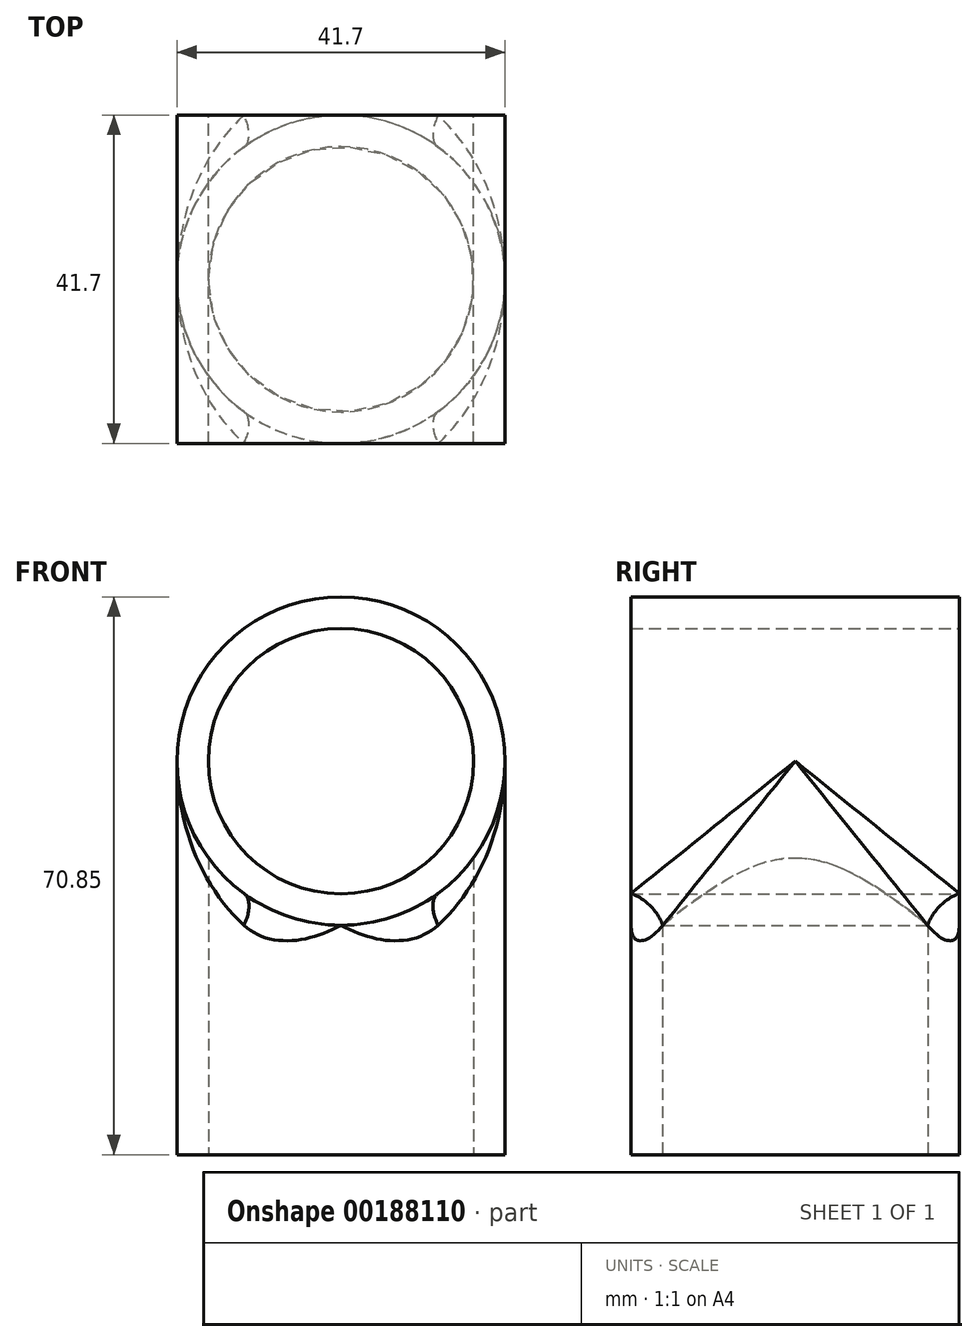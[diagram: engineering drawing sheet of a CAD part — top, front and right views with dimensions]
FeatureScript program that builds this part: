
annotation { "Feature Type Name" : "Feature", "Feature Type Description" : "" }
export const myFeature = defineFeature(function(context is Context, id is Id, definition is map)
    precondition{}
    {
        {
            var Q0;
            Q0=qCreatedBy(makeId("Top.planeOp"),FACE);
            var sketch = newSketch(context, id + "F0", { "sketchPlane" : qUnion([Q0])});
            skCircle(sketch, "E0", {"center": v(0, 0) * mm, "radius": 16.85 * mm});
            skCircle(sketch, "E1", {"center": v(0, 0) * mm, "radius": 20.85 * mm});
            skSolve(sketch);
        }
        {
            var Q0;
            Q0=makeQuery(id+"F0.imprint","IMPRINT",FACE,{"disambiguationData":[TD([[makeQuery(id+"F0.imprint","IMPRINT",EDGE,{"derivedFrom":sQuery(id+"F0.wireOp",EDGE,"E0")}),-1.0]])]});
            extrude(context, id + "F1", {"entities" : qUnion([Q0]), "depth" : 50 * mm});
        }
        {
            var Q0;
            Q0=makeQuery(id+"F1.opExtrude","CAP_FACE",FACE,{"disambiguationData":[OSD([sQuery(id+"F0.wireOp",EDGE,"E0"),sQuery(id+"F0.wireOp",EDGE,"E1")])],"isStart":false});
            var sketch = newSketch(context, id + "F2", { "sketchPlane" : qUnion([Q0])});
            skLineSegment(sketch, "E2.bottom", {"start": v(0, 20.85) * mm, "end": v(20.85, 20.85) * mm});
            skLineSegment(sketch, "E2.top", {"start": v(0, 0) * mm, "end": v(20.85, 0) * mm});
            skLineSegment(sketch, "E2.left", {"start": v(0, 20.85) * mm, "end": v(0, 0) * mm});
            skLineSegment(sketch, "E2.right", {"start": v(20.85, 20.85) * mm, "end": v(20.85, 0) * mm});
            skLineSegment(sketch, "E3.bottom", {"start": v(20.85, 0) * mm, "end": v(0, 0) * mm});
            skLineSegment(sketch, "E3.top", {"start": v(20.85, -20.85) * mm, "end": v(0, -20.85) * mm});
            skLineSegment(sketch, "E3.left", {"start": v(20.85, 0) * mm, "end": v(20.85, -20.85) * mm});
            skLineSegment(sketch, "E3.right", {"start": v(0, 0) * mm, "end": v(0, -20.85) * mm});
            skLineSegment(sketch, "E4", {"start": v(16.85, 0) * mm, "end": v(16.85, 20.85) * mm});
            skLineSegment(sketch, "E5", {"start": v(16.85, 0) * mm, "end": v(16.85, -20.85) * mm});
            skLineSegment(sketch, "E6", {"start": v(0, 20.85) * mm, "end": v(0, -20.85) * mm});
            skSolve(sketch);
        }
        {
            var Q0;
            {var subQ0=sQuery(id+"F2.wireOp",EDGE,"E2.right");Q0=makeQuery(id+"F2.imprint","IMPRINT",FACE,{"disambiguationData":[TD([[makeQuery(id+"F2.imprint","IMPRINT",EDGE,{"derivedFrom":subQ0}),-1.0]])]});}
            var Q1;
            {var subQ1=makeQuery(id+"F1.opExtrude","CAP_EDGE",EDGE,{"disambiguationData":[OSD([sQuery(id+"F0.wireOp",EDGE,"E1")])],"isStart":false});var subQ3=sQuery(id+"F2.wireOp",EDGE,"E4");var subQ5=makeQuery(id+"F2.imprint","INTERSECT",VERTEX,{"derivedFrom":[subQ1,subQ3]});Q1=makeQuery(id+"F2.imprint","IMPRINT",FACE,{"disambiguationData":[TD([[makeQuery(id+"F2.imprint","IMPRINT",EDGE,{"disambiguationData":[TD([[subQ5,1.0]])],"derivedFrom":subQ3}),-1.0]])]});}
            var Q2;
            {var subQ1=makeQuery(id+"F1.opExtrude","CAP_EDGE",EDGE,{"disambiguationData":[OSD([sQuery(id+"F0.wireOp",EDGE,"E1")])],"isStart":false});var subQ3=sQuery(id+"F2.wireOp",EDGE,"E5");var subQ5=makeQuery(id+"F2.imprint","INTERSECT",VERTEX,{"derivedFrom":[subQ1,subQ3]});Q2=makeQuery(id+"F2.imprint","IMPRINT",FACE,{"disambiguationData":[TD([[makeQuery(id+"F2.imprint","IMPRINT",EDGE,{"disambiguationData":[TD([[subQ5,1.0]])],"derivedFrom":subQ3}),1.0]])]});}
            var Q3;
            {var subQ0=sQuery(id+"F2.wireOp",EDGE,"E3.left");Q3=makeQuery(id+"F2.imprint","IMPRINT",FACE,{"disambiguationData":[TD([[makeQuery(id+"F2.imprint","IMPRINT",EDGE,{"derivedFrom":subQ0}),-1.0]])]});}
            var Q4;
            Q4=sQuery(id+"F2.wireOp",EDGE,"E6");
            revolve(context, id + "F3", {"operationType" : NewBodyOperationType.ADD, "entities" : qUnion([Q0, Q1, Q2, Q3]), "axis" : qUnion([Q4]), "revolveType" : RevolveType.FULL});
        }
        {
            var Q0;
            Q0=makeQuery(id+"F3.opRevolve","SWEPT_FACE",FACE,{"disambiguationData":[OSD([sQuery(id+"F2.wireOp",EDGE,"E2.bottom")])]});
            var sketch = newSketch(context, id + "F4", { "sketchPlane" : qUnion([Q0])});
            skCircle(sketch, "E7.0.0", {"center": v(0, 50) * mm, "radius": 20.85 * mm});
            skSolve(sketch);
        }
        {
            var Q0;
            Q0=makeQuery(id+"F4.imprint","IMPRINT",FACE,{"disambiguationData":[TD([[makeQuery(id+"F4.imprint","IMPRINT",EDGE,{"derivedFrom":makeQuery(id+"F3.opRevolve","SWEPT_EDGE",EDGE,{"disambiguationData":[OSD([sQuery(id+"F2.wireOp",EDGE,"E2.bottom"),sQuery(id+"F2.wireOp",EDGE,"E4")])]})}),1.0]])]});
            extrude(context, id + "F5", {"entities" : qUnion([Q0]), "operationType" : NewBodyOperationType.REMOVE, "endBound" : BoundingType.THROUGH_ALL, "oppositeDirection" : true, "depth" : 25 * mm});
        }
        {
            var Q0;
            Q0=makeQuery(id+"F0.imprint","IMPRINT",FACE,{"disambiguationData":[TD([[makeQuery(id+"F0.imprint","IMPRINT",EDGE,{"derivedFrom":sQuery(id+"F0.wireOp",EDGE,"E0")}),1.0]])]});
            var Q1;
            Q1=makeQuery(id+"F3.boolean.opBoolean","INTERSECT",VERTEX,{"disambiguationData":[OD(3.0)],"derivedFrom":[makeQuery(id+"F1.opExtrude","SWEPT_FACE",FACE,{"disambiguationData":[OSD([sQuery(id+"F0.wireOp",EDGE,"E1")])]}),makeQuery(id+"F3.opRevolve","SWEPT_FACE",FACE,{"disambiguationData":[OSD([sQuery(id+"F2.wireOp",EDGE,"E2.right"),sQuery(id+"F2.wireOp",EDGE,"E3.left")])]})]});
            extrude(context, id + "F6", {"entities" : qUnion([Q0]), "operationType" : NewBodyOperationType.REMOVE, "endBound" : BoundingType.UP_TO_VERTEX, "endBoundEntityVertex" : qUnion([Q1]), "depth" : 25 * mm});
        }
        {
            var Q0;
            Q0=makeQuery(id+"F3.boolean.opBoolean","INTERSECT",EDGE,{"disambiguationData":[OD(3.0)],"derivedFrom":[makeQuery(id+"F1.opExtrude","SWEPT_FACE",FACE,{"disambiguationData":[OSD([sQuery(id+"F0.wireOp",EDGE,"E1")])]}),makeQuery(id+"F3.opRevolve","SWEPT_FACE",FACE,{"disambiguationData":[OSD([sQuery(id+"F2.wireOp",EDGE,"E2.right"),sQuery(id+"F2.wireOp",EDGE,"E3.left")])]})]});
            var Q1;
            Q1=makeQuery(id+"F3.boolean.opBoolean","INTERSECT",EDGE,{"disambiguationData":[OD(1.0)],"derivedFrom":[makeQuery(id+"F1.opExtrude","SWEPT_FACE",FACE,{"disambiguationData":[OSD([sQuery(id+"F0.wireOp",EDGE,"E1")])]}),makeQuery(id+"F3.opRevolve","SWEPT_FACE",FACE,{"disambiguationData":[OSD([sQuery(id+"F2.wireOp",EDGE,"E2.right"),sQuery(id+"F2.wireOp",EDGE,"E3.left")])]})]});
            var Q2;
            {var subQ0=sQuery(id+"F0.wireOp",EDGE,"E0");var subQ1=sQuery(id+"F2.wireOp",EDGE,"E4");var subQ2=sQuery(id+"F2.wireOp",EDGE,"E2.bottom");var subQ3=sQuery(id+"F0.wireOp",EDGE,"E1");var subQ4=makeQuery(id+"F1.opExtrude","CAP_FACE",FACE,{"disambiguationData":[OSD([subQ0,subQ3])],"isStart":false});var subQ5=makeQuery(id+"F1.opExtrude","SWEPT_FACE",FACE,{"disambiguationData":[OSD([subQ0])]});var subQ6=makeQuery(id+"F3.opRevolve","SWEPT_FACE",FACE,{"disambiguationData":[OSD([subQ1,sQuery(id+"F2.wireOp",EDGE,"E5")])]});Q2=makeQuery(id+"F6.boolean.opBoolean","INTERSECT",EDGE,{"disambiguationData":[OD(1.0)],"derivedFrom":[makeQuery(id+"F5.boolean.opBoolean","MERGE",FACE,{"derivedFrom":[makeQuery(id+"F3.boolean.opBoolean","SPLIT",FACE,{"disambiguationData":[TD([subQ5,subQ4,subQ6])],"derivedFrom":subQ6}),makeQuery(id+"F3.boolean.opBoolean","SPLIT",FACE,{"disambiguationData":[TD([subQ5,subQ4,makeQuery(id+"F1.opExtrude","SWEPT_FACE",FACE,{"disambiguationData":[OSD([subQ3])]}),makeQuery(id+"F3.opRevolve","SWEPT_FACE",FACE,{"disambiguationData":[OSD([subQ2])]}),makeQuery(id+"F3.opRevolve","SWEPT_FACE",FACE,{"disambiguationData":[OSD([sQuery(id+"F2.wireOp",EDGE,"E3.top")])]}),subQ6])],"derivedFrom":subQ6}),makeQuery(id+"F5.opExtrude","SWEPT_FACE",FACE,{"disambiguationData":[OSD([subQ2,subQ1])]})]}),makeQuery(id+"F6.opExtrude","SWEPT_FACE",FACE,{"disambiguationData":[OSD([subQ0])]})]});}
            var Q3;
            {var subQ0=sQuery(id+"F0.wireOp",EDGE,"E0");var subQ1=sQuery(id+"F2.wireOp",EDGE,"E4");var subQ2=sQuery(id+"F2.wireOp",EDGE,"E2.bottom");var subQ3=sQuery(id+"F0.wireOp",EDGE,"E1");var subQ4=makeQuery(id+"F1.opExtrude","CAP_FACE",FACE,{"disambiguationData":[OSD([subQ0,subQ3])],"isStart":false});var subQ5=makeQuery(id+"F1.opExtrude","SWEPT_FACE",FACE,{"disambiguationData":[OSD([subQ0])]});var subQ6=makeQuery(id+"F3.opRevolve","SWEPT_FACE",FACE,{"disambiguationData":[OSD([subQ1,sQuery(id+"F2.wireOp",EDGE,"E5")])]});Q3=makeQuery(id+"F6.boolean.opBoolean","INTERSECT",EDGE,{"disambiguationData":[OD(0.0)],"derivedFrom":[makeQuery(id+"F5.boolean.opBoolean","MERGE",FACE,{"derivedFrom":[makeQuery(id+"F3.boolean.opBoolean","SPLIT",FACE,{"disambiguationData":[TD([subQ5,subQ4,subQ6])],"derivedFrom":subQ6}),makeQuery(id+"F3.boolean.opBoolean","SPLIT",FACE,{"disambiguationData":[TD([subQ5,subQ4,makeQuery(id+"F1.opExtrude","SWEPT_FACE",FACE,{"disambiguationData":[OSD([subQ3])]}),makeQuery(id+"F3.opRevolve","SWEPT_FACE",FACE,{"disambiguationData":[OSD([subQ2])]}),makeQuery(id+"F3.opRevolve","SWEPT_FACE",FACE,{"disambiguationData":[OSD([sQuery(id+"F2.wireOp",EDGE,"E3.top")])]}),subQ6])],"derivedFrom":subQ6}),makeQuery(id+"F5.opExtrude","SWEPT_FACE",FACE,{"disambiguationData":[OSD([subQ2,subQ1])]})]}),makeQuery(id+"F6.opExtrude","SWEPT_FACE",FACE,{"disambiguationData":[OSD([subQ0])]})]});}
            fillet(context, id + "F7", {"entities" : qUnion([Q0, Q1, Q2, Q3]), "radius" : 5 * mm, "tangentPropagation" : true, "allowEdgeOverflow" : false});
        }
    });
